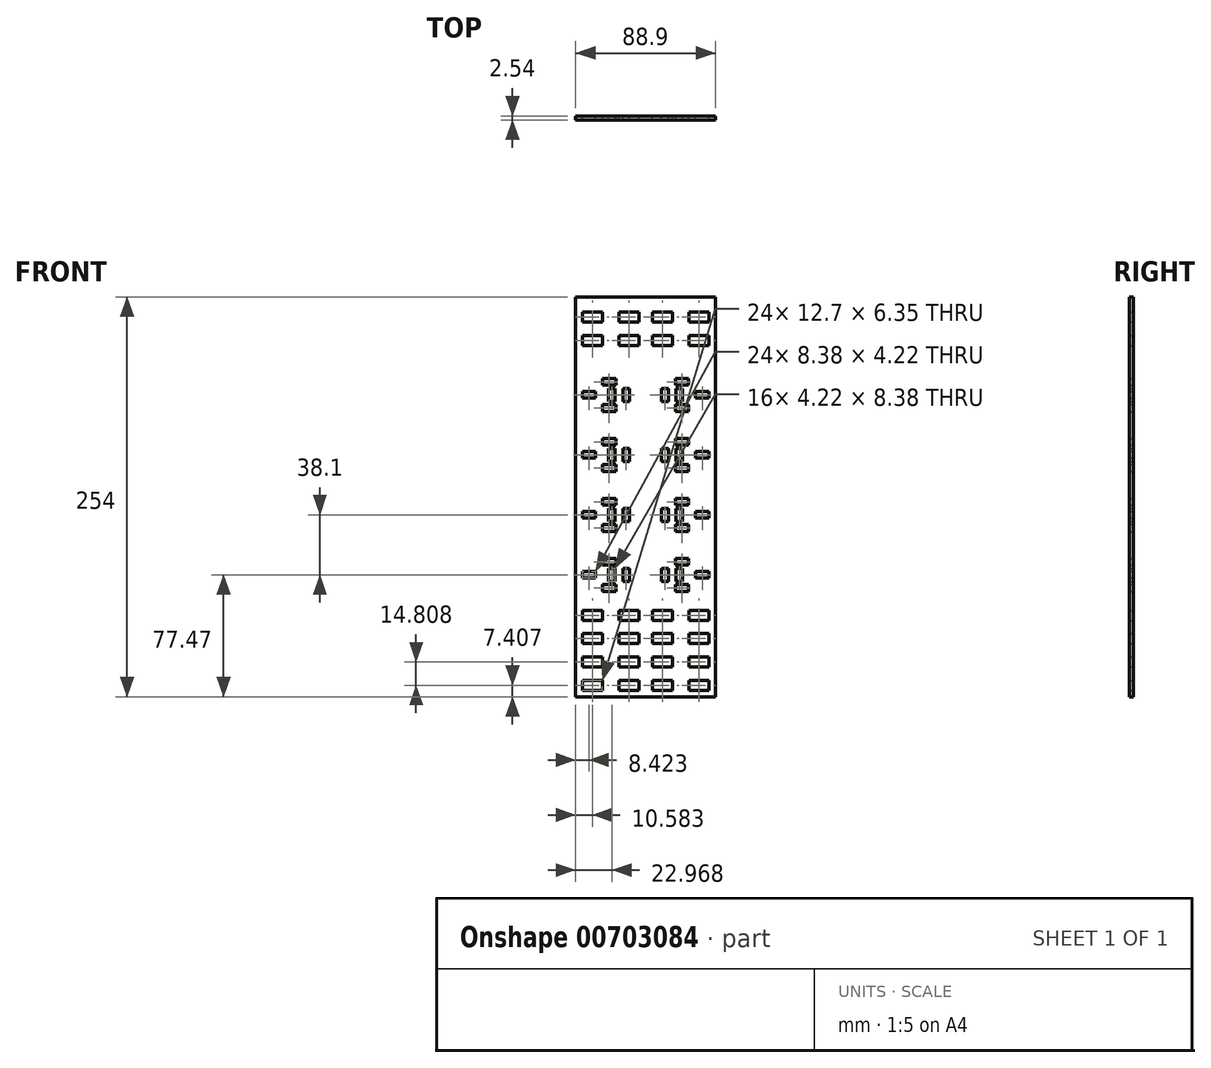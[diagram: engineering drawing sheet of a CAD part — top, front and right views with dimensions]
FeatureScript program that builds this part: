
annotation { "Feature Type Name" : "Feature", "Feature Type Description" : "" }
export const myFeature = defineFeature(function(context is Context, id is Id, definition is map)
    precondition{}
    {
        {
            var Q0;
            Q0=qCreatedBy(makeId("Front.planeOp"),FACE);
            var sketch = newSketch(context, id + "F0", { "sketchPlane" : qUnion([Q0])});
            skLineSegment(sketch, "E0.bottom", {"start": v(0, 254) * mm, "end": v(88.9, 254) * mm});
            skLineSegment(sketch, "E0.top", {"start": v(0, 0) * mm, "end": v(88.9, 0) * mm});
            skLineSegment(sketch, "E0.left", {"start": v(0, 254) * mm, "end": v(0, 0) * mm});
            skLineSegment(sketch, "E0.right", {"start": v(88.9, 254) * mm, "end": v(88.9, 0) * mm});
            skLineSegment(sketch, "E1.bottom", {"start": v(4.23, 10.58) * mm, "end": v(16.93, 10.58) * mm});
            skLineSegment(sketch, "E1.top", {"start": v(4.23, 4.23) * mm, "end": v(16.93, 4.23) * mm});
            skLineSegment(sketch, "E1.left", {"start": v(4.23, 10.58) * mm, "end": v(4.23, 4.23) * mm});
            skLineSegment(sketch, "E1.right", {"start": v(16.93, 10.58) * mm, "end": v(16.93, 4.23) * mm});
            skLineSegment(sketch, "E2.0.1.0", {"start": v(4.23, 25.39) * mm, "end": v(16.93, 25.39) * mm});
            skLineSegment(sketch, "E2.0.1.1", {"start": v(4.23, 25.39) * mm, "end": v(4.23, 19.04) * mm});
            skLineSegment(sketch, "E2.0.1.2", {"start": v(4.23, 19.04) * mm, "end": v(16.93, 19.04) * mm});
            skLineSegment(sketch, "E2.0.1.3", {"start": v(16.93, 25.39) * mm, "end": v(16.93, 19.04) * mm});
            skLineSegment(sketch, "E2.0.2.0", {"start": v(4.23, 40.2) * mm, "end": v(16.93, 40.2) * mm});
            skLineSegment(sketch, "E2.0.2.1", {"start": v(4.23, 40.2) * mm, "end": v(4.23, 33.85) * mm});
            skLineSegment(sketch, "E2.0.2.2", {"start": v(4.23, 33.85) * mm, "end": v(16.93, 33.85) * mm});
            skLineSegment(sketch, "E2.0.2.3", {"start": v(16.93, 40.2) * mm, "end": v(16.93, 33.85) * mm});
            skLineSegment(sketch, "E2.direction1", {"start": v(4.23, 10.58) * mm, "end": v(29.63, 10.58) * mm, "construction": true});
            skLineSegment(sketch, "E2.direction2", {"start": v(4.23, 10.58) * mm, "end": v(4.23, 25.39) * mm, "construction": true});
            skLineSegment(sketch, "E3.0.0.3", {"start": v(4.23, 55) * mm, "end": v(16.93, 55) * mm});
            skLineSegment(sketch, "E3.3.0.3", {"start": v(4.23, 55) * mm, "end": v(4.23, 48.66) * mm});
            skLineSegment(sketch, "E3.6.0.3", {"start": v(4.23, 48.66) * mm, "end": v(16.93, 48.66) * mm});
            skLineSegment(sketch, "E3.9.0.3", {"start": v(16.93, 55) * mm, "end": v(16.93, 48.66) * mm});
            skLineSegment(sketch, "E4", {"start": v(44.45, 0) * mm, "end": v(44.45, 254) * mm, "construction": true});
            skLineSegment(sketch, "E5.MirrorCS", {"start": v(84.67, 10.58) * mm, "end": v(71.97, 10.58) * mm});
            skLineSegment(sketch, "E6.MirrorCS", {"start": v(84.67, 4.23) * mm, "end": v(71.97, 4.23) * mm});
            skLineSegment(sketch, "E7.MirrorCS", {"start": v(84.67, 10.58) * mm, "end": v(84.67, 4.23) * mm});
            skLineSegment(sketch, "E8.MirrorCS", {"start": v(71.97, 10.58) * mm, "end": v(71.97, 4.23) * mm});
            skLineSegment(sketch, "E9.MirrorCS", {"start": v(84.67, 25.39) * mm, "end": v(84.67, 19.04) * mm});
            skLineSegment(sketch, "E10.MirrorCS", {"start": v(84.67, 55) * mm, "end": v(84.67, 48.66) * mm});
            skLineSegment(sketch, "E11.MirrorCS", {"start": v(84.67, 40.2) * mm, "end": v(84.67, 33.85) * mm});
            skLineSegment(sketch, "E12.MirrorCS", {"start": v(71.97, 55) * mm, "end": v(71.97, 48.66) * mm});
            skLineSegment(sketch, "E13.MirrorCS", {"start": v(84.67, 33.85) * mm, "end": v(71.97, 33.85) * mm});
            skLineSegment(sketch, "E14.MirrorCS", {"start": v(84.67, 10.58) * mm, "end": v(84.67, 25.39) * mm, "construction": true});
            skLineSegment(sketch, "E15.MirrorCS", {"start": v(71.97, 40.2) * mm, "end": v(71.97, 33.85) * mm});
            skLineSegment(sketch, "E16.MirrorCS", {"start": v(84.67, 55) * mm, "end": v(71.97, 55) * mm});
            skLineSegment(sketch, "E17.MirrorCS", {"start": v(84.67, 40.2) * mm, "end": v(71.97, 40.2) * mm});
            skLineSegment(sketch, "E18.MirrorCS", {"start": v(84.67, 48.66) * mm, "end": v(71.97, 48.66) * mm});
            skLineSegment(sketch, "E19.MirrorCS", {"start": v(84.67, 25.39) * mm, "end": v(71.97, 25.39) * mm});
            skLineSegment(sketch, "E20.MirrorCS", {"start": v(84.67, 19.04) * mm, "end": v(71.97, 19.04) * mm});
            skLineSegment(sketch, "E21.MirrorCS", {"start": v(71.97, 25.39) * mm, "end": v(71.97, 19.04) * mm});
            skLineSegment(sketch, "E22", {"start": v(44.45, 0) * mm, "end": v(0, 0) * mm, "construction": true});
            skLineSegment(sketch, "E23", {"start": v(22.23, 0) * mm, "end": v(22.23, 70.57) * mm, "construction": true});
            skLineSegment(sketch, "E24.MirrorCS", {"start": v(27.52, 40.2) * mm, "end": v(27.52, 33.85) * mm});
            skLineSegment(sketch, "E25.MirrorCS", {"start": v(40.22, 40.2) * mm, "end": v(40.22, 33.85) * mm});
            skLineSegment(sketch, "E26.MirrorCS", {"start": v(27.52, 25.39) * mm, "end": v(27.52, 19.04) * mm});
            skLineSegment(sketch, "E27.MirrorCS", {"start": v(40.22, 55) * mm, "end": v(40.22, 48.66) * mm});
            skLineSegment(sketch, "E28.MirrorCS", {"start": v(40.22, 25.39) * mm, "end": v(40.22, 19.04) * mm});
            skLineSegment(sketch, "E29.MirrorCS", {"start": v(27.52, 10.58) * mm, "end": v(27.52, 4.23) * mm});
            skLineSegment(sketch, "E30.MirrorCS", {"start": v(40.22, 10.58) * mm, "end": v(40.22, 4.23) * mm});
            skLineSegment(sketch, "E31.MirrorCS", {"start": v(27.52, 55) * mm, "end": v(27.52, 48.66) * mm});
            skLineSegment(sketch, "E32.MirrorCS", {"start": v(40.22, 10.58) * mm, "end": v(27.52, 10.58) * mm});
            skLineSegment(sketch, "E33.MirrorCS", {"start": v(40.22, 55) * mm, "end": v(27.52, 55) * mm});
            skLineSegment(sketch, "E34.MirrorCS", {"start": v(40.22, 48.66) * mm, "end": v(27.52, 48.66) * mm});
            skLineSegment(sketch, "E35.MirrorCS", {"start": v(40.22, 33.85) * mm, "end": v(27.52, 33.85) * mm});
            skLineSegment(sketch, "E36.MirrorCS", {"start": v(40.22, 40.2) * mm, "end": v(27.52, 40.2) * mm});
            skLineSegment(sketch, "E37.MirrorCS", {"start": v(40.22, 19.04) * mm, "end": v(27.52, 19.04) * mm});
            skLineSegment(sketch, "E38.MirrorCS", {"start": v(40.22, 25.39) * mm, "end": v(27.52, 25.39) * mm});
            skLineSegment(sketch, "E39.MirrorCS", {"start": v(40.22, 4.23) * mm, "end": v(27.52, 4.23) * mm});
            skLineSegment(sketch, "E40.MirrorCS", {"start": v(40.22, 10.58) * mm, "end": v(40.22, 25.39) * mm, "construction": true});
            skLineSegment(sketch, "E41", {"start": v(44.45, 0) * mm, "end": v(88.9, 0) * mm, "construction": true});
            skLineSegment(sketch, "E42", {"start": v(66.68, 0) * mm, "end": v(66.68, 68.1) * mm, "construction": true});
            skLineSegment(sketch, "E43.MirrorCS", {"start": v(48.68, 40.2) * mm, "end": v(48.68, 33.85) * mm});
            skLineSegment(sketch, "E44.MirrorCS", {"start": v(48.68, 10.58) * mm, "end": v(48.68, 4.23) * mm});
            skLineSegment(sketch, "E45.MirrorCS", {"start": v(61.38, 40.2) * mm, "end": v(61.38, 33.85) * mm});
            skLineSegment(sketch, "E46.MirrorCS", {"start": v(61.38, 10.58) * mm, "end": v(61.38, 4.23) * mm});
            skLineSegment(sketch, "E47.MirrorCS", {"start": v(48.68, 25.39) * mm, "end": v(48.68, 19.04) * mm});
            skLineSegment(sketch, "E48.MirrorCS", {"start": v(61.38, 25.39) * mm, "end": v(61.38, 19.04) * mm});
            skLineSegment(sketch, "E49.MirrorCS", {"start": v(61.38, 55) * mm, "end": v(61.38, 48.66) * mm});
            skLineSegment(sketch, "E50.MirrorCS", {"start": v(48.68, 55) * mm, "end": v(48.68, 48.66) * mm});
            skLineSegment(sketch, "E51.MirrorCS", {"start": v(48.68, 55) * mm, "end": v(61.38, 55) * mm});
            skLineSegment(sketch, "E52.MirrorCS", {"start": v(48.68, 10.58) * mm, "end": v(48.68, 25.39) * mm, "construction": true});
            skLineSegment(sketch, "E53.MirrorCS", {"start": v(48.68, 4.23) * mm, "end": v(61.38, 4.23) * mm});
            skLineSegment(sketch, "E54.MirrorCS", {"start": v(48.68, 25.39) * mm, "end": v(61.38, 25.39) * mm});
            skLineSegment(sketch, "E55.MirrorCS", {"start": v(48.68, 33.85) * mm, "end": v(61.38, 33.85) * mm});
            skLineSegment(sketch, "E56.MirrorCS", {"start": v(48.68, 10.58) * mm, "end": v(61.38, 10.58) * mm});
            skLineSegment(sketch, "E57.MirrorCS", {"start": v(48.68, 19.04) * mm, "end": v(61.38, 19.04) * mm});
            skLineSegment(sketch, "E58.MirrorCS", {"start": v(48.68, 48.66) * mm, "end": v(61.38, 48.66) * mm});
            skLineSegment(sketch, "E59.MirrorCS", {"start": v(48.68, 40.2) * mm, "end": v(61.38, 40.2) * mm});
            skLineSegment(sketch, "E60.bottom", {"start": v(4.23, 79.58) * mm, "end": v(12.61, 79.58) * mm});
            skLineSegment(sketch, "E60.top", {"start": v(4.23, 75.36) * mm, "end": v(12.61, 75.36) * mm});
            skLineSegment(sketch, "E60.left", {"start": v(4.23, 79.58) * mm, "end": v(4.23, 75.36) * mm});
            skLineSegment(sketch, "E60.right", {"start": v(12.61, 79.58) * mm, "end": v(12.61, 75.36) * mm});
            skLineSegment(sketch, "E61", {"start": v(4.23, 77.47) * mm, "end": v(41.36, 77.47) * mm, "construction": true});
            skLineSegment(sketch, "E62.MirrorCS", {"start": v(25.08, 73.28) * mm, "end": v(25.08, 81.66) * mm});
            skLineSegment(sketch, "E63.MirrorCS", {"start": v(20.86, 81.66) * mm, "end": v(25.08, 81.66) * mm});
            skLineSegment(sketch, "E64.MirrorCS", {"start": v(20.86, 73.28) * mm, "end": v(25.08, 73.28) * mm});
            skLineSegment(sketch, "E65.MirrorCS", {"start": v(20.86, 73.28) * mm, "end": v(20.86, 81.66) * mm});
            skLineSegment(sketch, "E66.bottom", {"start": v(17.12, 71.27) * mm, "end": v(25.5, 71.27) * mm});
            skLineSegment(sketch, "E66.top", {"start": v(17.12, 67.06) * mm, "end": v(25.5, 67.06) * mm});
            skLineSegment(sketch, "E66.left", {"start": v(17.12, 71.27) * mm, "end": v(17.12, 67.06) * mm});
            skLineSegment(sketch, "E66.right", {"start": v(25.5, 71.27) * mm, "end": v(25.5, 67.06) * mm});
            skLineSegment(sketch, "E67.bottom", {"start": v(17.12, 87.88) * mm, "end": v(25.5, 87.88) * mm});
            skLineSegment(sketch, "E67.top", {"start": v(17.12, 83.67) * mm, "end": v(25.5, 83.67) * mm});
            skLineSegment(sketch, "E67.left", {"start": v(17.12, 87.88) * mm, "end": v(17.12, 83.67) * mm});
            skLineSegment(sketch, "E67.right", {"start": v(25.5, 87.88) * mm, "end": v(25.5, 83.67) * mm});
            skLineSegment(sketch, "E68", {"start": v(17.12, 85.78) * mm, "end": v(31.12, 85.78) * mm, "construction": true});
            skLineSegment(sketch, "E69.MirrorCS", {"start": v(34.26, 73.28) * mm, "end": v(34.26, 81.66) * mm});
            skLineSegment(sketch, "E70.MirrorCS", {"start": v(30.05, 81.66) * mm, "end": v(34.26, 81.66) * mm});
            skLineSegment(sketch, "E71.MirrorCS", {"start": v(30.05, 73.28) * mm, "end": v(34.26, 73.28) * mm});
            skLineSegment(sketch, "E72.MirrorCS", {"start": v(30.05, 73.28) * mm, "end": v(30.05, 81.66) * mm});
            skPoint(sketch, "E73", {"position": v(20.86, 77.47) * mm});
            skPoint(sketch, "E74", {"position": v(30.05, 77.47) * mm});
            skLineSegment(sketch, "E75.MirrorCS", {"start": v(71.78, 87.88) * mm, "end": v(71.78, 83.67) * mm});
            skLineSegment(sketch, "E76.MirrorCS", {"start": v(68.04, 73.28) * mm, "end": v(63.82, 73.28) * mm});
            skLineSegment(sketch, "E77.MirrorCS", {"start": v(63.4, 87.88) * mm, "end": v(63.4, 83.67) * mm});
            skLineSegment(sketch, "E78.MirrorCS", {"start": v(68.04, 81.66) * mm, "end": v(63.82, 81.66) * mm});
            skLineSegment(sketch, "E79.MirrorCS", {"start": v(84.67, 79.58) * mm, "end": v(84.67, 75.36) * mm});
            skLineSegment(sketch, "E80.MirrorCS", {"start": v(68.04, 73.28) * mm, "end": v(68.04, 81.66) * mm});
            skLineSegment(sketch, "E81.MirrorCS", {"start": v(58.85, 73.28) * mm, "end": v(58.85, 81.66) * mm});
            skLineSegment(sketch, "E82.MirrorCS", {"start": v(71.78, 67.06) * mm, "end": v(63.4, 67.06) * mm});
            skPoint(sketch, "E83.MirrorP", {"position": v(68.04, 77.47) * mm});
            skLineSegment(sketch, "E84.MirrorCS", {"start": v(58.85, 81.66) * mm, "end": v(54.64, 81.66) * mm});
            skLineSegment(sketch, "E85.MirrorCS", {"start": v(71.78, 71.27) * mm, "end": v(63.4, 71.27) * mm});
            skLineSegment(sketch, "E86.MirrorCS", {"start": v(63.4, 71.27) * mm, "end": v(63.4, 67.06) * mm});
            skLineSegment(sketch, "E87.MirrorCS", {"start": v(63.82, 73.28) * mm, "end": v(63.82, 81.66) * mm});
            skLineSegment(sketch, "E88.MirrorCS", {"start": v(54.64, 73.28) * mm, "end": v(54.64, 81.66) * mm});
            skLineSegment(sketch, "E89.MirrorCS", {"start": v(84.67, 75.36) * mm, "end": v(76.29, 75.36) * mm});
            skLineSegment(sketch, "E90.MirrorCS", {"start": v(76.29, 79.58) * mm, "end": v(76.29, 75.36) * mm});
            skLineSegment(sketch, "E91.MirrorCS", {"start": v(71.78, 85.78) * mm, "end": v(57.78, 85.78) * mm, "construction": true});
            skLineSegment(sketch, "E92.MirrorCS", {"start": v(58.85, 73.28) * mm, "end": v(54.64, 73.28) * mm});
            skPoint(sketch, "E93.MirrorP", {"position": v(58.85, 77.47) * mm});
            skLineSegment(sketch, "E94.MirrorCS", {"start": v(84.67, 79.58) * mm, "end": v(76.29, 79.58) * mm});
            skLineSegment(sketch, "E95.MirrorCS", {"start": v(71.78, 87.88) * mm, "end": v(63.4, 87.88) * mm});
            skLineSegment(sketch, "E96.MirrorCS", {"start": v(71.78, 83.67) * mm, "end": v(63.4, 83.67) * mm});
            skLineSegment(sketch, "E97.MirrorCS", {"start": v(71.78, 71.27) * mm, "end": v(71.78, 67.06) * mm});
            skLineSegment(sketch, "E98.0.1.0", {"start": v(17.12, 123.88) * mm, "end": v(31.12, 123.88) * mm, "construction": true});
            skLineSegment(sketch, "E98.0.1.1", {"start": v(71.78, 125.98) * mm, "end": v(63.4, 125.98) * mm});
            skLineSegment(sketch, "E98.0.1.2", {"start": v(71.78, 123.88) * mm, "end": v(57.78, 123.88) * mm, "construction": true});
            skLineSegment(sketch, "E98.0.1.3", {"start": v(71.78, 105.16) * mm, "end": v(63.4, 105.16) * mm});
            skLineSegment(sketch, "E98.0.1.4", {"start": v(4.23, 117.68) * mm, "end": v(12.61, 117.68) * mm});
            skLineSegment(sketch, "E98.0.1.5", {"start": v(54.64, 111.38) * mm, "end": v(54.64, 119.76) * mm});
            skPoint(sketch, "E98.0.1.6", {"position": v(68.04, 115.57) * mm});
            skLineSegment(sketch, "E98.0.1.7", {"start": v(71.78, 109.37) * mm, "end": v(63.4, 109.37) * mm});
            skLineSegment(sketch, "E98.0.1.8", {"start": v(63.82, 111.38) * mm, "end": v(63.82, 119.76) * mm});
            skLineSegment(sketch, "E98.0.1.9", {"start": v(84.67, 117.68) * mm, "end": v(76.29, 117.68) * mm});
            skLineSegment(sketch, "E98.0.1.10", {"start": v(4.23, 113.46) * mm, "end": v(12.61, 113.46) * mm});
            skLineSegment(sketch, "E98.0.1.11", {"start": v(34.26, 111.38) * mm, "end": v(34.26, 119.76) * mm});
            skLineSegment(sketch, "E98.0.1.12", {"start": v(71.78, 121.77) * mm, "end": v(63.4, 121.77) * mm});
            skLineSegment(sketch, "E98.0.1.13", {"start": v(17.12, 121.77) * mm, "end": v(25.5, 121.77) * mm});
            skLineSegment(sketch, "E98.0.1.14", {"start": v(17.12, 125.98) * mm, "end": v(25.5, 125.98) * mm});
            skLineSegment(sketch, "E98.0.1.15", {"start": v(17.12, 109.37) * mm, "end": v(25.5, 109.37) * mm});
            skPoint(sketch, "E98.0.1.16", {"position": v(58.85, 115.57) * mm});
            skPoint(sketch, "E98.0.1.17", {"position": v(30.05, 115.57) * mm});
            skLineSegment(sketch, "E98.0.1.18", {"start": v(25.08, 111.38) * mm, "end": v(25.08, 119.76) * mm});
            skLineSegment(sketch, "E98.0.1.19", {"start": v(17.12, 105.16) * mm, "end": v(25.5, 105.16) * mm});
            skLineSegment(sketch, "E98.0.1.20", {"start": v(84.67, 113.46) * mm, "end": v(76.29, 113.46) * mm});
            skPoint(sketch, "E98.0.1.21", {"position": v(20.86, 115.57) * mm});
            skLineSegment(sketch, "E98.0.1.22", {"start": v(4.23, 115.57) * mm, "end": v(41.36, 115.57) * mm, "construction": true});
            skLineSegment(sketch, "E98.0.1.23", {"start": v(58.85, 111.38) * mm, "end": v(58.85, 119.76) * mm});
            skLineSegment(sketch, "E98.0.1.24", {"start": v(30.05, 111.38) * mm, "end": v(30.05, 119.76) * mm});
            skLineSegment(sketch, "E98.0.1.25", {"start": v(20.86, 111.38) * mm, "end": v(20.86, 119.76) * mm});
            skLineSegment(sketch, "E98.0.1.26", {"start": v(68.04, 111.38) * mm, "end": v(68.04, 119.76) * mm});
            skLineSegment(sketch, "E98.0.1.27", {"start": v(25.5, 109.37) * mm, "end": v(25.5, 105.16) * mm});
            skLineSegment(sketch, "E98.0.1.28", {"start": v(63.4, 125.98) * mm, "end": v(63.4, 121.77) * mm});
            skLineSegment(sketch, "E98.0.1.29", {"start": v(68.04, 119.76) * mm, "end": v(63.82, 119.76) * mm});
            skLineSegment(sketch, "E98.0.1.30", {"start": v(58.85, 111.38) * mm, "end": v(54.64, 111.38) * mm});
            skLineSegment(sketch, "E98.0.1.31", {"start": v(63.4, 109.37) * mm, "end": v(63.4, 105.16) * mm});
            skLineSegment(sketch, "E98.0.1.32", {"start": v(68.04, 111.38) * mm, "end": v(63.82, 111.38) * mm});
            skLineSegment(sketch, "E98.0.1.33", {"start": v(25.5, 125.98) * mm, "end": v(25.5, 121.77) * mm});
            skLineSegment(sketch, "E98.0.1.34", {"start": v(58.85, 119.76) * mm, "end": v(54.64, 119.76) * mm});
            skLineSegment(sketch, "E98.0.1.35", {"start": v(17.12, 125.98) * mm, "end": v(17.12, 121.77) * mm});
            skLineSegment(sketch, "E98.0.1.36", {"start": v(20.86, 111.38) * mm, "end": v(25.08, 111.38) * mm});
            skLineSegment(sketch, "E98.0.1.37", {"start": v(71.78, 125.98) * mm, "end": v(71.78, 121.77) * mm});
            skLineSegment(sketch, "E98.0.1.38", {"start": v(12.61, 117.68) * mm, "end": v(12.61, 113.46) * mm});
            skLineSegment(sketch, "E98.0.1.39", {"start": v(20.86, 119.76) * mm, "end": v(25.08, 119.76) * mm});
            skLineSegment(sketch, "E98.0.1.40", {"start": v(84.67, 117.68) * mm, "end": v(84.67, 113.46) * mm});
            skLineSegment(sketch, "E98.0.1.41", {"start": v(71.78, 109.37) * mm, "end": v(71.78, 105.16) * mm});
            skLineSegment(sketch, "E98.0.1.42", {"start": v(30.05, 119.76) * mm, "end": v(34.26, 119.76) * mm});
            skLineSegment(sketch, "E98.0.1.43", {"start": v(17.12, 109.37) * mm, "end": v(17.12, 105.16) * mm});
            skLineSegment(sketch, "E98.0.1.44", {"start": v(76.29, 117.68) * mm, "end": v(76.29, 113.46) * mm});
            skLineSegment(sketch, "E98.0.1.45", {"start": v(30.05, 111.38) * mm, "end": v(34.26, 111.38) * mm});
            skLineSegment(sketch, "E98.0.1.46", {"start": v(4.23, 117.68) * mm, "end": v(4.23, 113.46) * mm});
            skLineSegment(sketch, "E98.0.2.0", {"start": v(17.12, 161.98) * mm, "end": v(31.12, 161.98) * mm, "construction": true});
            skLineSegment(sketch, "E98.0.2.1", {"start": v(71.78, 164.08) * mm, "end": v(63.4, 164.08) * mm});
            skLineSegment(sketch, "E98.0.2.2", {"start": v(71.78, 161.98) * mm, "end": v(57.78, 161.98) * mm, "construction": true});
            skLineSegment(sketch, "E98.0.2.3", {"start": v(71.78, 143.26) * mm, "end": v(63.4, 143.26) * mm});
            skLineSegment(sketch, "E98.0.2.4", {"start": v(4.23, 155.78) * mm, "end": v(12.61, 155.78) * mm});
            skLineSegment(sketch, "E98.0.2.5", {"start": v(54.64, 149.48) * mm, "end": v(54.64, 157.86) * mm});
            skPoint(sketch, "E98.0.2.6", {"position": v(68.04, 153.67) * mm});
            skLineSegment(sketch, "E98.0.2.7", {"start": v(71.78, 147.47) * mm, "end": v(63.4, 147.47) * mm});
            skLineSegment(sketch, "E98.0.2.8", {"start": v(63.82, 149.48) * mm, "end": v(63.82, 157.86) * mm});
            skLineSegment(sketch, "E98.0.2.9", {"start": v(84.67, 155.78) * mm, "end": v(76.29, 155.78) * mm});
            skLineSegment(sketch, "E98.0.2.10", {"start": v(4.23, 151.56) * mm, "end": v(12.61, 151.56) * mm});
            skLineSegment(sketch, "E98.0.2.11", {"start": v(34.26, 149.48) * mm, "end": v(34.26, 157.86) * mm});
            skLineSegment(sketch, "E98.0.2.12", {"start": v(71.78, 159.87) * mm, "end": v(63.4, 159.87) * mm});
            skLineSegment(sketch, "E98.0.2.13", {"start": v(17.12, 159.87) * mm, "end": v(25.5, 159.87) * mm});
            skLineSegment(sketch, "E98.0.2.14", {"start": v(17.12, 164.08) * mm, "end": v(25.5, 164.08) * mm});
            skLineSegment(sketch, "E98.0.2.15", {"start": v(17.12, 147.47) * mm, "end": v(25.5, 147.47) * mm});
            skPoint(sketch, "E98.0.2.16", {"position": v(58.85, 153.67) * mm});
            skPoint(sketch, "E98.0.2.17", {"position": v(30.05, 153.67) * mm});
            skLineSegment(sketch, "E98.0.2.18", {"start": v(25.08, 149.48) * mm, "end": v(25.08, 157.86) * mm});
            skLineSegment(sketch, "E98.0.2.19", {"start": v(17.12, 143.26) * mm, "end": v(25.5, 143.26) * mm});
            skLineSegment(sketch, "E98.0.2.20", {"start": v(84.67, 151.56) * mm, "end": v(76.29, 151.56) * mm});
            skPoint(sketch, "E98.0.2.21", {"position": v(20.86, 153.67) * mm});
            skLineSegment(sketch, "E98.0.2.22", {"start": v(4.23, 153.67) * mm, "end": v(41.36, 153.67) * mm, "construction": true});
            skLineSegment(sketch, "E98.0.2.23", {"start": v(58.85, 149.48) * mm, "end": v(58.85, 157.86) * mm});
            skLineSegment(sketch, "E98.0.2.24", {"start": v(30.05, 149.48) * mm, "end": v(30.05, 157.86) * mm});
            skLineSegment(sketch, "E98.0.2.25", {"start": v(20.86, 149.48) * mm, "end": v(20.86, 157.86) * mm});
            skLineSegment(sketch, "E98.0.2.26", {"start": v(68.04, 149.48) * mm, "end": v(68.04, 157.86) * mm});
            skLineSegment(sketch, "E98.0.2.27", {"start": v(25.5, 147.47) * mm, "end": v(25.5, 143.26) * mm});
            skLineSegment(sketch, "E98.0.2.28", {"start": v(63.4, 164.08) * mm, "end": v(63.4, 159.87) * mm});
            skLineSegment(sketch, "E98.0.2.29", {"start": v(68.04, 157.86) * mm, "end": v(63.82, 157.86) * mm});
            skLineSegment(sketch, "E98.0.2.30", {"start": v(58.85, 149.48) * mm, "end": v(54.64, 149.48) * mm});
            skLineSegment(sketch, "E98.0.2.31", {"start": v(63.4, 147.47) * mm, "end": v(63.4, 143.26) * mm});
            skLineSegment(sketch, "E98.0.2.32", {"start": v(68.04, 149.48) * mm, "end": v(63.82, 149.48) * mm});
            skLineSegment(sketch, "E98.0.2.33", {"start": v(25.5, 164.08) * mm, "end": v(25.5, 159.87) * mm});
            skLineSegment(sketch, "E98.0.2.34", {"start": v(58.85, 157.86) * mm, "end": v(54.64, 157.86) * mm});
            skLineSegment(sketch, "E98.0.2.35", {"start": v(17.12, 164.08) * mm, "end": v(17.12, 159.87) * mm});
            skLineSegment(sketch, "E98.0.2.36", {"start": v(20.86, 149.48) * mm, "end": v(25.08, 149.48) * mm});
            skLineSegment(sketch, "E98.0.2.37", {"start": v(71.78, 164.08) * mm, "end": v(71.78, 159.87) * mm});
            skLineSegment(sketch, "E98.0.2.38", {"start": v(12.61, 155.78) * mm, "end": v(12.61, 151.56) * mm});
            skLineSegment(sketch, "E98.0.2.39", {"start": v(20.86, 157.86) * mm, "end": v(25.08, 157.86) * mm});
            skLineSegment(sketch, "E98.0.2.40", {"start": v(84.67, 155.78) * mm, "end": v(84.67, 151.56) * mm});
            skLineSegment(sketch, "E98.0.2.41", {"start": v(71.78, 147.47) * mm, "end": v(71.78, 143.26) * mm});
            skLineSegment(sketch, "E98.0.2.42", {"start": v(30.05, 157.86) * mm, "end": v(34.26, 157.86) * mm});
            skLineSegment(sketch, "E98.0.2.43", {"start": v(17.12, 147.47) * mm, "end": v(17.12, 143.26) * mm});
            skLineSegment(sketch, "E98.0.2.44", {"start": v(76.29, 155.78) * mm, "end": v(76.29, 151.56) * mm});
            skLineSegment(sketch, "E98.0.2.45", {"start": v(30.05, 149.48) * mm, "end": v(34.26, 149.48) * mm});
            skLineSegment(sketch, "E98.0.2.46", {"start": v(4.23, 155.78) * mm, "end": v(4.23, 151.56) * mm});
            skLineSegment(sketch, "E98.0.3.0", {"start": v(17.12, 200.08) * mm, "end": v(31.12, 200.08) * mm, "construction": true});
            skLineSegment(sketch, "E98.0.3.1", {"start": v(71.78, 202.18) * mm, "end": v(63.4, 202.18) * mm});
            skLineSegment(sketch, "E98.0.3.2", {"start": v(71.78, 200.08) * mm, "end": v(57.78, 200.08) * mm, "construction": true});
            skLineSegment(sketch, "E98.0.3.3", {"start": v(71.78, 181.36) * mm, "end": v(63.4, 181.36) * mm});
            skLineSegment(sketch, "E98.0.3.4", {"start": v(4.23, 193.88) * mm, "end": v(12.61, 193.88) * mm});
            skLineSegment(sketch, "E98.0.3.5", {"start": v(54.64, 187.58) * mm, "end": v(54.64, 195.96) * mm});
            skPoint(sketch, "E98.0.3.6", {"position": v(68.04, 191.77) * mm});
            skLineSegment(sketch, "E98.0.3.7", {"start": v(71.78, 185.57) * mm, "end": v(63.4, 185.57) * mm});
            skLineSegment(sketch, "E98.0.3.8", {"start": v(63.82, 187.58) * mm, "end": v(63.82, 195.96) * mm});
            skLineSegment(sketch, "E98.0.3.9", {"start": v(84.67, 193.88) * mm, "end": v(76.29, 193.88) * mm});
            skLineSegment(sketch, "E98.0.3.10", {"start": v(4.23, 189.66) * mm, "end": v(12.61, 189.66) * mm});
            skLineSegment(sketch, "E98.0.3.11", {"start": v(34.26, 187.58) * mm, "end": v(34.26, 195.96) * mm});
            skLineSegment(sketch, "E98.0.3.12", {"start": v(71.78, 197.97) * mm, "end": v(63.4, 197.97) * mm});
            skLineSegment(sketch, "E98.0.3.13", {"start": v(17.12, 197.97) * mm, "end": v(25.5, 197.97) * mm});
            skLineSegment(sketch, "E98.0.3.14", {"start": v(17.12, 202.18) * mm, "end": v(25.5, 202.18) * mm});
            skLineSegment(sketch, "E98.0.3.15", {"start": v(17.12, 185.57) * mm, "end": v(25.5, 185.57) * mm});
            skPoint(sketch, "E98.0.3.16", {"position": v(58.85, 191.77) * mm});
            skPoint(sketch, "E98.0.3.17", {"position": v(30.05, 191.77) * mm});
            skLineSegment(sketch, "E98.0.3.18", {"start": v(25.08, 187.58) * mm, "end": v(25.08, 195.96) * mm});
            skLineSegment(sketch, "E98.0.3.19", {"start": v(17.12, 181.36) * mm, "end": v(25.5, 181.36) * mm});
            skLineSegment(sketch, "E98.0.3.20", {"start": v(84.67, 189.66) * mm, "end": v(76.29, 189.66) * mm});
            skPoint(sketch, "E98.0.3.21", {"position": v(20.86, 191.77) * mm});
            skLineSegment(sketch, "E98.0.3.22", {"start": v(4.23, 191.77) * mm, "end": v(41.36, 191.77) * mm, "construction": true});
            skLineSegment(sketch, "E98.0.3.23", {"start": v(58.85, 187.58) * mm, "end": v(58.85, 195.96) * mm});
            skLineSegment(sketch, "E98.0.3.24", {"start": v(30.05, 187.58) * mm, "end": v(30.05, 195.96) * mm});
            skLineSegment(sketch, "E98.0.3.25", {"start": v(20.86, 187.58) * mm, "end": v(20.86, 195.96) * mm});
            skLineSegment(sketch, "E98.0.3.26", {"start": v(68.04, 187.58) * mm, "end": v(68.04, 195.96) * mm});
            skLineSegment(sketch, "E98.0.3.27", {"start": v(25.5, 185.57) * mm, "end": v(25.5, 181.36) * mm});
            skLineSegment(sketch, "E98.0.3.28", {"start": v(63.4, 202.18) * mm, "end": v(63.4, 197.97) * mm});
            skLineSegment(sketch, "E98.0.3.29", {"start": v(68.04, 195.96) * mm, "end": v(63.82, 195.96) * mm});
            skLineSegment(sketch, "E98.0.3.30", {"start": v(58.85, 187.58) * mm, "end": v(54.64, 187.58) * mm});
            skLineSegment(sketch, "E98.0.3.31", {"start": v(63.4, 185.57) * mm, "end": v(63.4, 181.36) * mm});
            skLineSegment(sketch, "E98.0.3.32", {"start": v(68.04, 187.58) * mm, "end": v(63.82, 187.58) * mm});
            skLineSegment(sketch, "E98.0.3.33", {"start": v(25.5, 202.18) * mm, "end": v(25.5, 197.97) * mm});
            skLineSegment(sketch, "E98.0.3.34", {"start": v(58.85, 195.96) * mm, "end": v(54.64, 195.96) * mm});
            skLineSegment(sketch, "E98.0.3.35", {"start": v(17.12, 202.18) * mm, "end": v(17.12, 197.97) * mm});
            skLineSegment(sketch, "E98.0.3.36", {"start": v(20.86, 187.58) * mm, "end": v(25.08, 187.58) * mm});
            skLineSegment(sketch, "E98.0.3.37", {"start": v(71.78, 202.18) * mm, "end": v(71.78, 197.97) * mm});
            skLineSegment(sketch, "E98.0.3.38", {"start": v(12.61, 193.88) * mm, "end": v(12.61, 189.66) * mm});
            skLineSegment(sketch, "E98.0.3.39", {"start": v(20.86, 195.96) * mm, "end": v(25.08, 195.96) * mm});
            skLineSegment(sketch, "E98.0.3.40", {"start": v(84.67, 193.88) * mm, "end": v(84.67, 189.66) * mm});
            skLineSegment(sketch, "E98.0.3.41", {"start": v(71.78, 185.57) * mm, "end": v(71.78, 181.36) * mm});
            skLineSegment(sketch, "E98.0.3.42", {"start": v(30.05, 195.96) * mm, "end": v(34.26, 195.96) * mm});
            skLineSegment(sketch, "E98.0.3.43", {"start": v(17.12, 185.57) * mm, "end": v(17.12, 181.36) * mm});
            skLineSegment(sketch, "E98.0.3.44", {"start": v(76.29, 193.88) * mm, "end": v(76.29, 189.66) * mm});
            skLineSegment(sketch, "E98.0.3.45", {"start": v(30.05, 187.58) * mm, "end": v(34.26, 187.58) * mm});
            skLineSegment(sketch, "E98.0.3.46", {"start": v(4.23, 193.88) * mm, "end": v(4.23, 189.66) * mm});
            skLineSegment(sketch, "E98.direction1", {"start": v(4.23, 75.36) * mm, "end": v(29.63, 75.36) * mm, "construction": true});
            skLineSegment(sketch, "E98.direction2", {"start": v(4.23, 75.36) * mm, "end": v(4.23, 113.46) * mm, "construction": true});
            skLineSegment(sketch, "E99", {"start": v(0, 139.07) * mm, "end": v(88.9, 139.07) * mm, "construction": true});
            skLineSegment(sketch, "E100.MirrorCS", {"start": v(84.67, 223.14) * mm, "end": v(84.67, 229.49) * mm});
            skLineSegment(sketch, "E101.MirrorCS", {"start": v(40.22, 237.94) * mm, "end": v(40.22, 244.3) * mm});
            skLineSegment(sketch, "E102.MirrorCS", {"start": v(48.68, 237.94) * mm, "end": v(48.68, 244.3) * mm});
            skLineSegment(sketch, "E103.MirrorCS", {"start": v(4.23, 237.94) * mm, "end": v(4.23, 244.3) * mm});
            skLineSegment(sketch, "E104.MirrorCS", {"start": v(71.97, 223.14) * mm, "end": v(71.97, 229.49) * mm});
            skLineSegment(sketch, "E105.MirrorCS", {"start": v(16.93, 237.94) * mm, "end": v(16.93, 244.3) * mm});
            skLineSegment(sketch, "E106.MirrorCS", {"start": v(61.38, 237.94) * mm, "end": v(61.38, 244.3) * mm});
            skLineSegment(sketch, "E107.MirrorCS", {"start": v(40.22, 223.14) * mm, "end": v(40.22, 229.49) * mm});
            skLineSegment(sketch, "E108.MirrorCS", {"start": v(48.68, 223.14) * mm, "end": v(48.68, 229.49) * mm});
            skLineSegment(sketch, "E109.MirrorCS", {"start": v(84.67, 237.94) * mm, "end": v(84.67, 244.3) * mm});
            skLineSegment(sketch, "E110.MirrorCS", {"start": v(27.52, 237.94) * mm, "end": v(27.52, 244.3) * mm});
            skLineSegment(sketch, "E111.MirrorCS", {"start": v(4.23, 223.14) * mm, "end": v(4.23, 229.49) * mm});
            skLineSegment(sketch, "E112.MirrorCS", {"start": v(16.93, 223.14) * mm, "end": v(16.93, 229.49) * mm});
            skLineSegment(sketch, "E113.MirrorCS", {"start": v(71.97, 237.94) * mm, "end": v(71.97, 244.3) * mm});
            skLineSegment(sketch, "E114.MirrorCS", {"start": v(61.38, 223.14) * mm, "end": v(61.38, 229.49) * mm});
            skLineSegment(sketch, "E115.MirrorCS", {"start": v(27.52, 223.14) * mm, "end": v(27.52, 229.49) * mm});
            skLineSegment(sketch, "E116.MirrorCS", {"start": v(48.68, 237.94) * mm, "end": v(61.38, 237.94) * mm});
            skLineSegment(sketch, "E117.MirrorCS", {"start": v(48.68, 229.49) * mm, "end": v(61.38, 229.49) * mm});
            skLineSegment(sketch, "E118.MirrorCS", {"start": v(4.23, 244.3) * mm, "end": v(16.93, 244.3) * mm});
            skLineSegment(sketch, "E119.MirrorCS", {"start": v(84.67, 244.3) * mm, "end": v(71.97, 244.3) * mm});
            skLineSegment(sketch, "E120.MirrorCS", {"start": v(48.68, 244.3) * mm, "end": v(61.38, 244.3) * mm});
            skLineSegment(sketch, "E121.MirrorCS", {"start": v(84.67, 223.14) * mm, "end": v(71.97, 223.14) * mm});
            skLineSegment(sketch, "E122.MirrorCS", {"start": v(4.23, 223.14) * mm, "end": v(16.93, 223.14) * mm});
            skLineSegment(sketch, "E123.MirrorCS", {"start": v(84.67, 229.49) * mm, "end": v(71.97, 229.49) * mm});
            skLineSegment(sketch, "E124.MirrorCS", {"start": v(40.22, 229.49) * mm, "end": v(27.52, 229.49) * mm});
            skLineSegment(sketch, "E125.MirrorCS", {"start": v(48.68, 223.14) * mm, "end": v(61.38, 223.14) * mm});
            skLineSegment(sketch, "E126.MirrorCS", {"start": v(4.23, 229.49) * mm, "end": v(16.93, 229.49) * mm});
            skLineSegment(sketch, "E127.MirrorCS", {"start": v(4.23, 237.94) * mm, "end": v(16.93, 237.94) * mm});
            skLineSegment(sketch, "E128.MirrorCS", {"start": v(84.67, 237.94) * mm, "end": v(71.97, 237.94) * mm});
            skLineSegment(sketch, "E129.MirrorCS", {"start": v(40.22, 237.94) * mm, "end": v(27.52, 237.94) * mm});
            skLineSegment(sketch, "E130.MirrorCS", {"start": v(40.22, 223.14) * mm, "end": v(27.52, 223.14) * mm});
            skLineSegment(sketch, "E131.MirrorCS", {"start": v(40.22, 244.3) * mm, "end": v(27.52, 244.3) * mm});
            skSolve(sketch);
        }
        {
            var Q0;
            Q0 = qSketchRegion(id + "F0", true);
            extrude(context, id + "F1", {"entities" : qUnion([Q0]), "depth" : 2.54 * mm, "offsetDistance" : 25.4 * mm});
        }
    });
